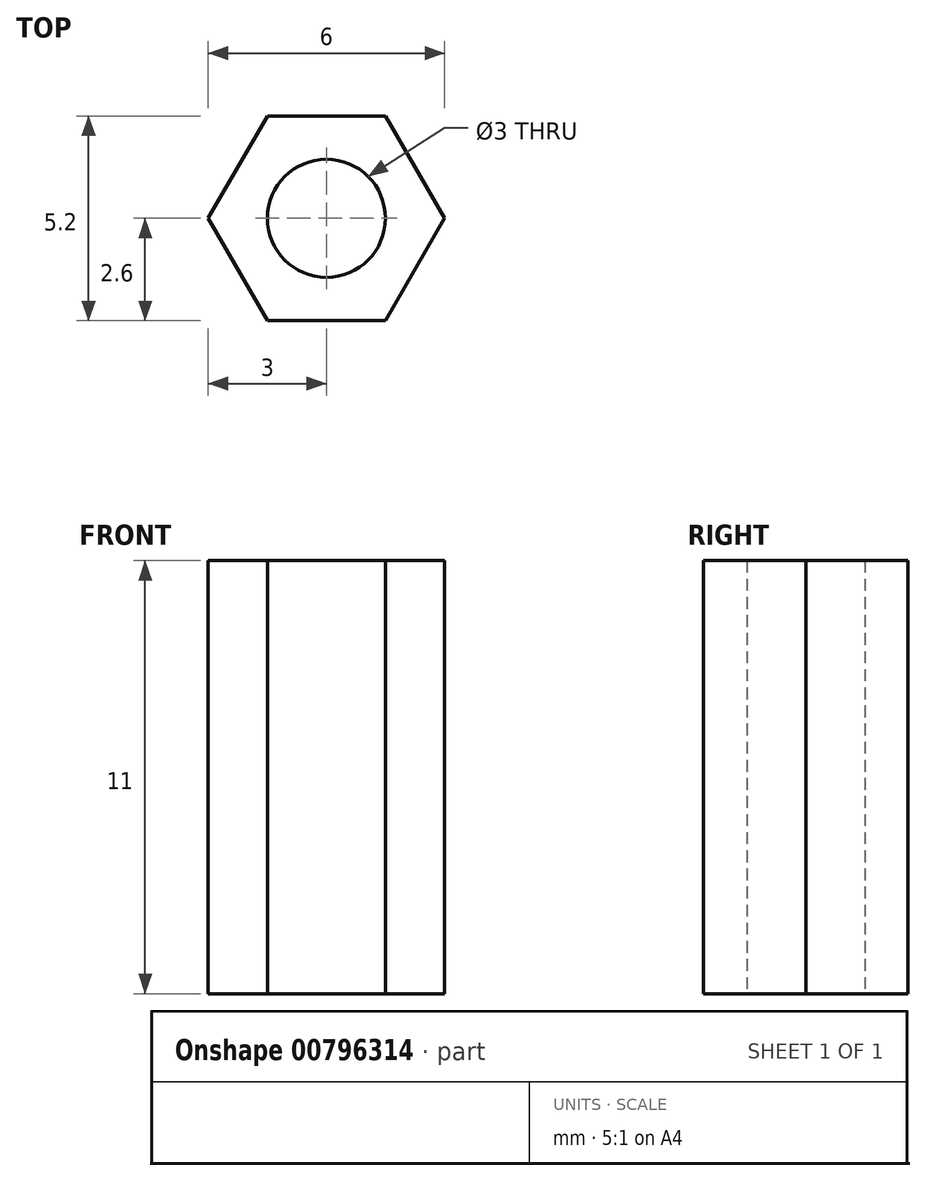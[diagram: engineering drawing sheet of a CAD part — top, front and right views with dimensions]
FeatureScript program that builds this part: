
annotation { "Feature Type Name" : "Feature", "Feature Type Description" : "" }
export const myFeature = defineFeature(function(context is Context, id is Id, definition is map)
    precondition{}
    {
        {
            var Q0;
            Q0=qCreatedBy(makeId("Top.planeOp"),FACE);
            var sketch = newSketch(context, id + "F0", { "sketchPlane" : qUnion([Q0])});
            skCircle(sketch, "E0", {"center": v(0, 0) * mm, "radius": 1.5 * mm});
            skCircle(sketch, "E1.cCircle", {"center": v(0, 0) * mm, "radius": 3 * mm, "construction": true});
            skLineSegment(sketch, "E1.0", {"start": v(3, 0) * mm, "end": v(1.5, -2.6) * mm});
            skLineSegment(sketch, "E1.1", {"start": v(1.5, -2.6) * mm, "end": v(-1.5, -2.6) * mm});
            skLineSegment(sketch, "E1.2", {"start": v(-1.5, -2.6) * mm, "end": v(-3, 0) * mm});
            skLineSegment(sketch, "E1.3", {"start": v(-3, 0) * mm, "end": v(-1.5, 2.6) * mm});
            skLineSegment(sketch, "E1.4", {"start": v(-1.5, 2.6) * mm, "end": v(1.5, 2.6) * mm});
            skLineSegment(sketch, "E1.5", {"start": v(1.5, 2.6) * mm, "end": v(3, 0) * mm});
            skSolve(sketch);
        }
        {
            var Q0;
            Q0=makeQuery(id+"F0.imprint","IMPRINT",FACE,{"disambiguationData":[TD([[makeQuery(id+"F0.imprint","IMPRINT",EDGE,{"derivedFrom":sQuery(id+"F0.wireOp",EDGE,"E0")}),-1.0]])]});
            extrude(context, id + "F1", {"entities" : qUnion([Q0]), "depth" : 11 * mm, "offsetDistance" : 25 * mm});
        }
    });
